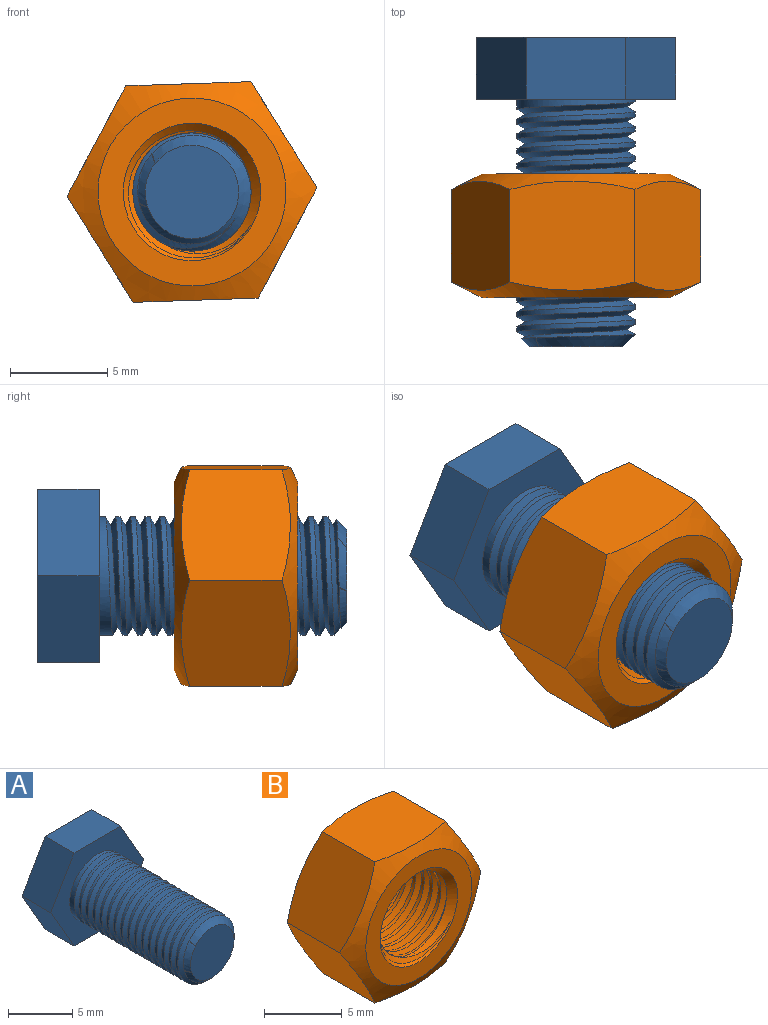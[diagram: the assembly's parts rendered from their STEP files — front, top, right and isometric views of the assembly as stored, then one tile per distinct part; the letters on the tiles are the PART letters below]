
ASSEMBLY  parts=2 mates=1
PART A: 17 faces, bbox 10.3x16x8.9 mm
  f0: cylinder r=3.04mm len=12.07mm, axis (0,1,0), area 55.9mm2, adj f9,f13,f14,f15,f16
  f1: plane 10.27x8.89mm, normal (0,1,0), area 60.4mm2, adj f3,f4,f5,f6,f7,f8,f10,f11
  f2: plane 4.8x4.8mm, normal (0,-1,0), area 18.1mm2, adj f13
  f3: plane 4.45x3.18mm, normal (-0.87,0,0.5), area 16.3mm2, adj f1,f4,f8,f9
  f4: plane 5.13x3.18mm, normal (0,0,1), area 16.3mm2, adj f1,f3,f5,f9
  f5: plane 4.45x3.18mm, normal (0.87,0,0.5), area 16.3mm2, adj f1,f4,f6,f9
  f6: plane 4.45x3.18mm, normal (0.87,0,-0.5), area 16.3mm2, adj f1,f5,f7,f9
  f7: plane 5.13x3.18mm, normal (0,0,-1), area 16.3mm2, adj f1,f6,f8,f9
  f8: plane 4.45x3.18mm, normal (-0.87,0,-0.5), area 16.3mm2, adj f1,f3,f7,f9
  f9: plane 10.27x8.89mm, normal (0,-1,0), area 39.5mm2, adj f0,f3,f4,f5,f6,f7,f8
  f10: cylinder r=4.9mm len=6.35mm, axis (0,0,-1), area 8.8mm2, adj f1,f11,f12
  f11: plane 6.35x1.17mm, normal (0,0,-1), area 5.1mm2, adj f1,f10
  f12: plane 6.35x1.17mm, normal (0,0,1), area 5.1mm2, adj f1,f10
  f13: cone r=2.4mm half-angle=45deg, axis (0,1,0), area 11.6mm2, adj f0,f2,f15,f16
  f14: plane 0.51x0.38mm, normal (0.87,0,0.5), area 0.1mm2, adj f0,f15,f16
  f15: bspline ~12.7x7.01mm, area 143.8mm2, adj f0,f13,f14,f16
  f16: bspline ~12.7x7.01mm, area 140.4mm2, adj f0,f13,f14,f15
PART B: 17 faces, bbox 13.4x7.1x13.4 mm
  f0: cone r=3.53mm half-angle=45deg, axis (0,1,0), area 11.8mm2, adj f2,f3,f14,f15
  f1: plane 9.65x9.65mm, normal (0,-1,0), area 34mm2, adj f5,f13
  f2: plane 9.65x9.65mm, normal (0,1,0), area 34mm2, adj f0,f4
  f3: cylinder r=3.02mm len=6.05mm, axis (0,1,0), area 33.6mm2, adj f0,f12,f13,f15,f16
  f4: cone r=4.32mm half-angle=63.4deg, axis (0,-1,0), area 39.1mm2, adj f2,f6,f7,f8,f9,f10,f11
  f5: cone r=8.13mm half-angle=63.4deg, axis (0,1,0), area 38mm2, adj f1,f6,f7,f8,f9,f10,f11
  f6: plane 5.62x5.56mm, normal (0.87,0,-0.5), area 34.2mm2, adj f4,f5,f7,f11
  f7: plane 6.94x6.13mm, normal (0,0,-1), area 34.2mm2, adj f4,f5,f6,f8
  f8: plane 5.62x5.56mm, normal (-0.87,0,-0.5), area 34.2mm2, adj f4,f5,f7,f9
  f9: plane 5.62x5.56mm, normal (-0.87,0,0.5), area 34.2mm2, adj f4,f5,f8,f10
  f10: plane 6.43x5.62mm, normal (0,0,1), area 34.2mm2, adj f4,f5,f9,f11
  f11: plane 5.62x5.56mm, normal (0.87,0,0.5), area 34.2mm2, adj f4,f5,f6,f10
  f12: cone r=3.02mm half-angle=45deg, axis (0,-1,0), area 0.2mm2, adj f3,f13,f15
  f13: cone r=3.02mm half-angle=45deg, axis (0,-1,0), area 10.5mm2, adj f1,f3,f12,f15,f16
  f14: plane 0.44x0.32mm, normal (0,0,1), area 0mm2, adj f0,f15,f16
  f15: bspline ~8x6.93mm, area 78.2mm2, adj f0,f3,f12,f13,f14,f16
  f16: bspline ~8x6.93mm, area 77.2mm2, adj f3,f13,f14,f15
PLACE A t=(-0.25,-1.54,1.36)mm fixed
PLACE B rot(axis=(0,-1,0),1.9deg) t=(-0.25,-2.21,1.36)mm
MATE cylindrical B.f0 <-> A.f0  axis (0,-1,0) through (-0.25,-5.38,1.36)mm
